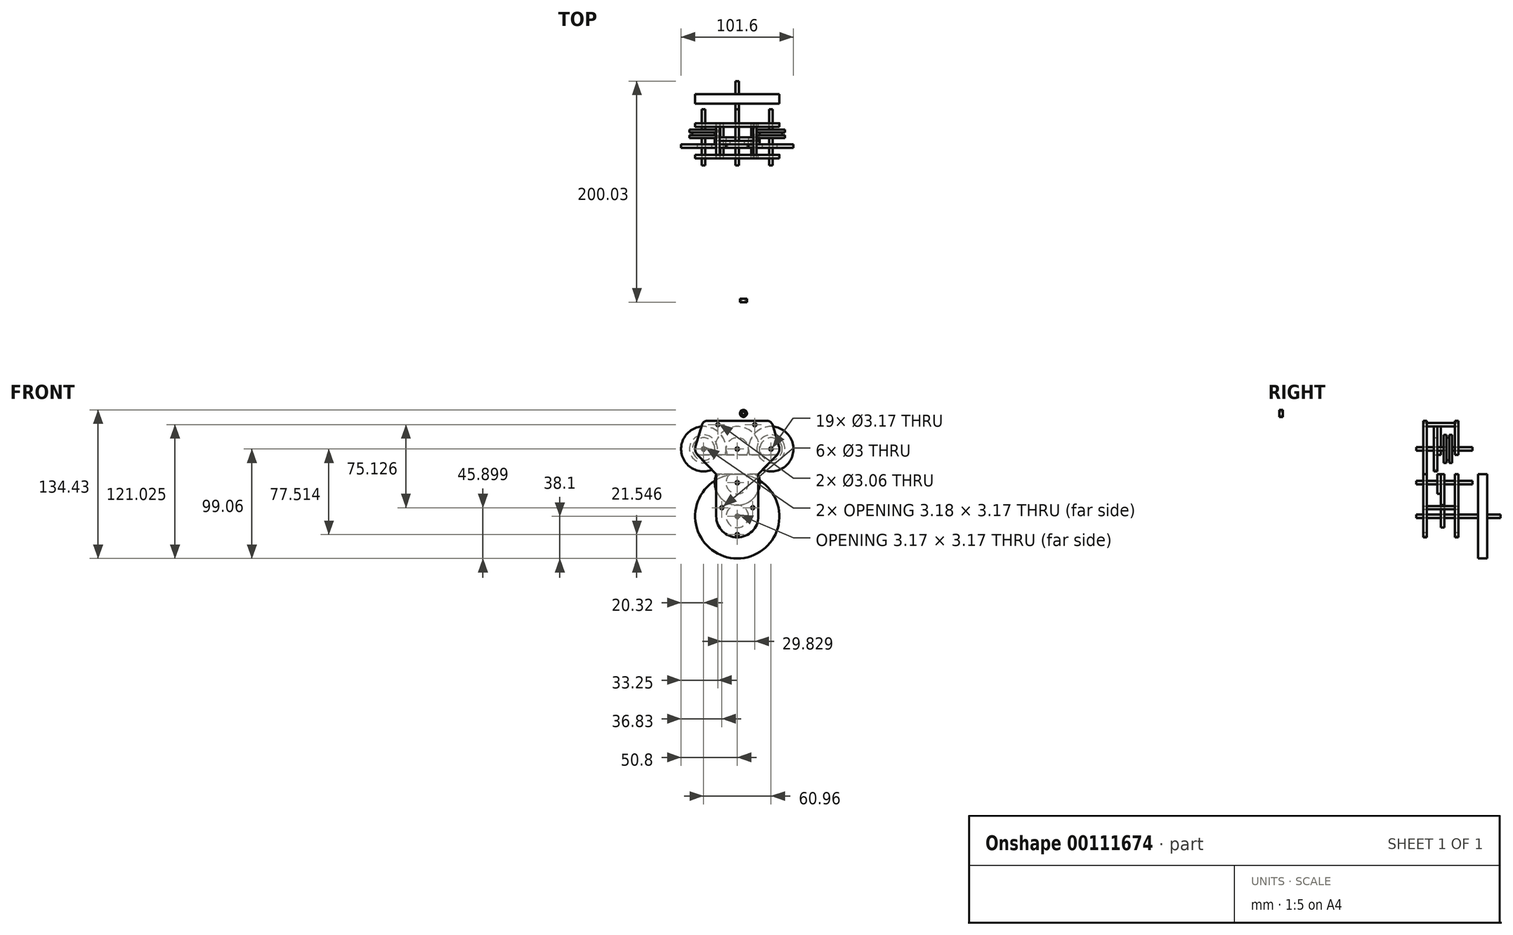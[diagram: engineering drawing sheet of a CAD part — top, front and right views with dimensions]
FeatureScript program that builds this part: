
annotation { "Feature Type Name" : "Feature", "Feature Type Description" : "" }
export const myFeature = defineFeature(function(context is Context, id is Id, definition is map)
    precondition{}
    {
        {
            var Q0;
            Q0=qCreatedBy(makeId("Front.planeOp"),FACE);
            var sketch = newSketch(context, id + "F0", { "sketchPlane" : qUnion([Q0])});
            skLineSegment(sketch, "E0", {"start": v(0, 0) * mm, "end": v(0, -60.96) * mm});
            skCircle(sketch, "E1", {"center": v(0, -60.96) * mm, "radius": 10.16 * mm});
            skCircle(sketch, "E2", {"center": v(0, -30.48) * mm, "radius": 20.32 * mm});
            skCircle(sketch, "E3", {"center": v(0, -30.48) * mm, "radius": 10.16 * mm});
            skCircle(sketch, "E4", {"center": v(0, 0) * mm, "radius": 20.32 * mm});
            skCircle(sketch, "E5", {"center": v(0, 0) * mm, "radius": 10.16 * mm});
            skLineSegment(sketch, "E6", {"start": v(0, 0) * mm, "end": v(30.48, 0) * mm});
            skLineSegment(sketch, "E7", {"start": v(30.48, 0) * mm, "end": v(-30.48, 0) * mm});
            skCircle(sketch, "E8", {"center": v(-30.48, 0) * mm, "radius": 20.32 * mm});
            skCircle(sketch, "E9", {"center": v(30.48, 0) * mm, "radius": 20.32 * mm});
            skCircle(sketch, "E10", {"center": v(-30.48, 0) * mm, "radius": 1.59 * mm});
            skCircle(sketch, "E11", {"center": v(0, 0) * mm, "radius": 1.59 * mm});
            skCircle(sketch, "E12", {"center": v(30.48, 0) * mm, "radius": 1.59 * mm});
            skCircle(sketch, "E13", {"center": v(0, -30.48) * mm, "radius": 1.59 * mm});
            skCircle(sketch, "E14", {"center": v(0, -60.96) * mm, "radius": 1.59 * mm});
            skSolve(sketch);
        }
        {
            var Q0;
            Q0=qCreatedBy(makeId("Front.planeOp"),FACE);
            cPlane(context, id + "F1", {"entities" : qUnion([Q0]), "cplaneType" : CPlaneType.OFFSET, "offset" : 3.17 * mm, "width" : 152.4 * mm, "height" : 152.4 * mm});
        }
        {
            var Q0;
            Q0=qCreatedBy(id+"F1.planeOp",FACE);
            var sketch = newSketch(context, id + "F2", { "sketchPlane" : qUnion([Q0])});
            skCircle(sketch, "E15.0", {"center": v(0, 0) * mm, "radius": 1.59 * mm});
            skCircle(sketch, "E16.0", {"center": v(30.48, 0) * mm, "radius": 1.59 * mm});
            skCircle(sketch, "E17.0", {"center": v(-30.48, 0) * mm, "radius": 1.59 * mm});
            skCircle(sketch, "E18.0", {"center": v(0, -30.48) * mm, "radius": 1.59 * mm});
            skCircle(sketch, "E19.0", {"center": v(0, -60.96) * mm, "radius": 1.59 * mm});
            skLineSegment(sketch, "E20", {"start": v(-30.9, 25.53) * mm, "end": v(30.73, 25.48) * mm});
            skCircle(sketch, "E21", {"center": v(0, -60.96) * mm, "radius": 19.05 * mm});
            skLineSegment(sketch, "E22", {"start": v(0, -60.96) * mm, "end": v(-19.05, -60.96) * mm});
            skLineSegment(sketch, "E23", {"start": v(0, -60.96) * mm, "end": v(19.05, -60.96) * mm});
            skLineSegment(sketch, "E24", {"start": v(19.05, -60.96) * mm, "end": v(19.05, -22.68) * mm});
            skLineSegment(sketch, "E25", {"start": v(-19.05, -60.96) * mm, "end": v(-19.05, -22.68) * mm});
            skCircle(sketch, "E26", {"center": v(30.48, 0) * mm, "radius": 7.62 * mm});
            skCircle(sketch, "E27", {"center": v(-30.48, 0) * mm, "radius": 7.62 * mm});
            skLineSegment(sketch, "E28", {"start": v(37.77, 2.2) * mm, "end": v(30.73, 25.48) * mm});
            skLineSegment(sketch, "E29", {"start": v(-30.9, 25.53) * mm, "end": v(-37.79, 2.15) * mm});
            skLineSegment(sketch, "E30", {"start": v(-35.94, -5.31) * mm, "end": v(-19.05, -22.68) * mm});
            skLineSegment(sketch, "E31", {"start": v(19.05, -22.68) * mm, "end": v(35.94, -5.31) * mm});
            skLineSegment(sketch, "E32", {"start": v(-0.09, 25.5) * mm, "end": v(0, 0) * mm});
            skCircle(sketch, "E33", {"center": v(15.86, 21.96) * mm, "radius": 1.5 * mm});
            skCircle(sketch, "E34", {"center": v(-17.55, 21.96) * mm, "radius": 1.5 * mm});
            skLineSegment(sketch, "E35", {"start": v(0, -53.16) * mm, "end": v(13.97, -53.16) * mm});
            skLineSegment(sketch, "E36", {"start": v(0, -53.16) * mm, "end": v(-13.97, -53.16) * mm});
            skCircle(sketch, "E37", {"center": v(13.97, -53.16) * mm, "radius": 1.5 * mm});
            skCircle(sketch, "E38", {"center": v(-13.97, -53.16) * mm, "radius": 1.5 * mm});
            skSolve(sketch);
        }
        {
            var Q0;
            Q0 = qSketchRegion(id + "F2", true);
            extrude(context, id + "F3", {"entities" : qUnion([Q0]), "depth" : 3.17 * mm});
        }
        {
            var Q0;
            Q0=makeQuery(id+"F3.opExtrude","CAP_FACE",FACE,{"disambiguationData":[OSD([sQuery(id+"F2.wireOp",EDGE,"E15.0"),sQuery(id+"F2.wireOp",EDGE,"E16.0"),sQuery(id+"F2.wireOp",EDGE,"E17.0"),sQuery(id+"F2.wireOp",EDGE,"E18.0"),sQuery(id+"F2.wireOp",EDGE,"E19.0"),sQuery(id+"F2.wireOp",EDGE,"DBtKeoEe-sxFA-O8Cd-5S0k-6v0tE5dEFOVB"),sQuery(id+"F2.wireOp",EDGE,"FIhjvamt-jRJC-0Qks-E5rB-tkHqEzlwZ8Zz"),sQuery(id+"F2.wireOp",EDGE,"KFKZsqRK-ZnOK-MkHf-qwN2-OSyO8BWJYoXi"),sQuery(id+"F2.wireOp",EDGE,"E20"),sQuery(id+"F2.wireOp",EDGE,"WcMJ8zR9-ZSbF-q2kM-oJpC-Lqe6jbKvmUBf"),sQuery(id+"F2.wireOp",EDGE,"RShMeTTQ-3lLB-r0UE-RSKj-mqnAByZPcrAj")])],"isStart":false});
            cPlane(context, id + "F4", {"entities" : qUnion([Q0]), "cplaneType" : CPlaneType.OFFSET, "offset" : 25.4 * mm, "width" : 152.4 * mm, "height" : 152.4 * mm});
        }
        {
            var Q0;
            Q0=qCreatedBy(id+"F4.planeOp",FACE);
            var sketch = newSketch(context, id + "F5", { "sketchPlane" : qUnion([Q0])});
            skCircle(sketch, "E39.0", {"center": v(-30.48, 0) * mm, "radius": 1.59 * mm});
            skCircle(sketch, "E40.0", {"center": v(0, 0) * mm, "radius": 1.59 * mm});
            skCircle(sketch, "E41.0", {"center": v(30.48, 0) * mm, "radius": 1.59 * mm});
            skCircle(sketch, "E42.0", {"center": v(0, -30.48) * mm, "radius": 1.59 * mm});
            skCircle(sketch, "E43.0", {"center": v(0, -60.96) * mm, "radius": 1.59 * mm});
            skLineSegment(sketch, "E44.0", {"start": v(19.05, -60.96) * mm, "end": v(19.05, -22.68) * mm});
            skArc(sketch, "E45.0", {"start": v(-19.05, -60.96) * mm, "mid": v(0, -80) * mm, "end": v(19.05, -60.96) * mm});
            skLineSegment(sketch, "E46.0", {"start": v(-19.05, -60.96) * mm, "end": v(-19.05, -22.68) * mm});
            skLineSegment(sketch, "E47.0", {"start": v(-35.94, -5.31) * mm, "end": v(-19.05, -22.68) * mm});
            skArc(sketch, "E48.0", {"start": v(-37.79, 2.15) * mm, "mid": v(-37.88, -1.83) * mm, "end": v(-35.94, -5.31) * mm});
            skLineSegment(sketch, "E49.0", {"start": v(-30.9, 25.53) * mm, "end": v(-37.79, 2.15) * mm});
            skLineSegment(sketch, "E50.0", {"start": v(-30.9, 25.53) * mm, "end": v(30.73, 25.48) * mm});
            skLineSegment(sketch, "E51.0", {"start": v(37.77, 2.2) * mm, "end": v(30.73, 25.48) * mm});
            skLineSegment(sketch, "E52.0", {"start": v(19.05, -22.68) * mm, "end": v(35.94, -5.31) * mm});
            skArc(sketch, "E53.0", {"start": v(35.94, -5.31) * mm, "mid": v(37.88, -1.8) * mm, "end": v(37.77, 2.2) * mm});
            skCircle(sketch, "E54.0", {"center": v(-17.55, 21.96) * mm, "radius": 1.5 * mm});
            skCircle(sketch, "E55.0", {"center": v(15.86, 21.96) * mm, "radius": 1.5 * mm});
            skCircle(sketch, "E56.0", {"center": v(-13.97, -53.16) * mm, "radius": 1.5 * mm});
            skCircle(sketch, "E57.0", {"center": v(13.97, -53.16) * mm, "radius": 1.5 * mm});
            skSolve(sketch);
        }
        {
            var Q0;
            Q0 = qSketchRegion(id + "F5", true);
            extrude(context, id + "F6", {"entities" : qUnion([Q0]), "depth" : 3.17 * mm});
        }
        {
            var Q0;
            Q0=makeQuery(id+"F2.imprint","IMPRINT",FACE,{"disambiguationData":[TD([[makeQuery(id+"F2.imprint","IMPRINT",EDGE,{"derivedFrom":sQuery(id+"F2.wireOp",EDGE,"E33")}),1.0]])]});
            extrude(context, id + "F7", {"entities" : qUnion([Q0]), "depth" : 0.25 * mm});
        }
        {
            var Q0;
            Q0=makeQuery(id+"F7.opExtrude","CAP_FACE",FACE,{"disambiguationData":[OSD([sQuery(id+"F2.wireOp",EDGE,"E33")])],"isStart":true});
            extrude(context, id + "F8", {"entities" : qUnion([Q0]), "operationType" : NewBodyOperationType.REMOVE, "oppositeDirection" : true, "depth" : 25.4 * mm});
        }
        {
            var Q0;
            Q0=makeQuery(id+"F3.opExtrude","CAP_FACE",FACE,{"disambiguationData":[OSD([sQuery(id+"F2.wireOp",EDGE,"E15.0"),sQuery(id+"F2.wireOp",EDGE,"E16.0"),sQuery(id+"F2.wireOp",EDGE,"E17.0"),sQuery(id+"F2.wireOp",EDGE,"E18.0"),sQuery(id+"F2.wireOp",EDGE,"E19.0"),sQuery(id+"F2.wireOp",EDGE,"E20"),sQuery(id+"F2.wireOp",EDGE,"E21"),sQuery(id+"F2.wireOp",EDGE,"E24"),sQuery(id+"F2.wireOp",EDGE,"E25"),sQuery(id+"F2.wireOp",EDGE,"E26"),sQuery(id+"F2.wireOp",EDGE,"E27"),sQuery(id+"F2.wireOp",EDGE,"E28"),sQuery(id+"F2.wireOp",EDGE,"E29"),sQuery(id+"F2.wireOp",EDGE,"E30"),sQuery(id+"F2.wireOp",EDGE,"E31"),sQuery(id+"F2.wireOp",EDGE,"E33"),sQuery(id+"F2.wireOp",EDGE,"E34"),sQuery(id+"F2.wireOp",EDGE,"E37"),sQuery(id+"F2.wireOp",EDGE,"E38")])],"isStart":true});
            cPlane(context, id + "F9", {"entities" : qUnion([Q0]), "cplaneType" : CPlaneType.OFFSET, "offset" : 7.62 * mm, "width" : 152.4 * mm, "height" : 152.4 * mm});
        }
        {
            var Q0;
            Q0=makeQuery(id+"F6.opExtrude","CAP_FACE",FACE,{"disambiguationData":[OSD([sQuery(id+"F5.wireOp",EDGE,"E39.0"),sQuery(id+"F5.wireOp",EDGE,"E40.0"),sQuery(id+"F5.wireOp",EDGE,"E41.0"),sQuery(id+"F5.wireOp",EDGE,"E42.0"),sQuery(id+"F5.wireOp",EDGE,"E43.0"),sQuery(id+"F5.wireOp",EDGE,"E44.0"),sQuery(id+"F5.wireOp",EDGE,"E45.0"),sQuery(id+"F5.wireOp",EDGE,"E46.0"),sQuery(id+"F5.wireOp",EDGE,"E47.0"),sQuery(id+"F5.wireOp",EDGE,"E48.0"),sQuery(id+"F5.wireOp",EDGE,"E49.0"),sQuery(id+"F5.wireOp",EDGE,"E50.0"),sQuery(id+"F5.wireOp",EDGE,"E51.0"),sQuery(id+"F5.wireOp",EDGE,"E52.0"),sQuery(id+"F5.wireOp",EDGE,"E53.0"),sQuery(id+"F5.wireOp",EDGE,"E54.0"),sQuery(id+"F5.wireOp",EDGE,"E55.0"),sQuery(id+"F5.wireOp",EDGE,"E56.0"),sQuery(id+"F5.wireOp",EDGE,"E57.0")])],"isStart":true});
            cPlane(context, id + "F10", {"entities" : qUnion([Q0]), "cplaneType" : CPlaneType.OFFSET, "offset" : 12.7 * mm, "width" : 152.4 * mm, "height" : 152.4 * mm});
        }
        {
            var Q0;
            Q0=qCreatedBy(id+"F10.planeOp",FACE);
            var sketch = newSketch(context, id + "F11", { "sketchPlane" : qUnion([Q0])});
            skCircle(sketch, "E58.0", {"center": v(0, -30.48) * mm, "radius": 1.59 * mm});
            skCircle(sketch, "E59.0", {"center": v(0, -60.96) * mm, "radius": 1.59 * mm});
            skCircle(sketch, "E60.0", {"center": v(0, -60.96) * mm, "radius": 10.16 * mm});
            skCircle(sketch, "E61.0", {"center": v(0, -30.48) * mm, "radius": 20.32 * mm});
            skSolve(sketch);
        }
        {
            var Q0;
            Q0 = qSketchRegion(id + "F11", true);
            extrude(context, id + "F12", {"entities" : qUnion([Q0]), "depth" : 3.17 * mm});
        }
        {
            var Q0;
            Q0=makeQuery(id+"F12.opExtrude","CAP_FACE",FACE,{"disambiguationData":[OSD([sQuery(id+"F11.wireOp",EDGE,"E58.0"),sQuery(id+"F11.wireOp",EDGE,"E61.0")])],"isStart":true});
            var sketch = newSketch(context, id + "F13", { "sketchPlane" : qUnion([Q0])});
            skCircle(sketch, "E62.0", {"center": v(0, -30.48) * mm, "radius": 10.16 * mm});
            skCircle(sketch, "E63.0", {"center": v(0, -30.48) * mm, "radius": 1.59 * mm});
            skCircle(sketch, "E64.0", {"center": v(0, 0) * mm, "radius": 1.59 * mm});
            skCircle(sketch, "E65.0", {"center": v(0, 0) * mm, "radius": 20.32 * mm});
            skSolve(sketch);
        }
        {
            var Q0;
            Q0 = qSketchRegion(id + "F13", true);
            extrude(context, id + "F14", {"entities" : qUnion([Q0]), "depth" : 3.17 * mm});
        }
        {
            var Q0;
            Q0=makeQuery(id+"F14.opExtrude","CAP_FACE",FACE,{"disambiguationData":[OSD([sQuery(id+"F13.wireOp",EDGE,"E64.0"),sQuery(id+"F13.wireOp",EDGE,"E65.0")])],"isStart":false});
            var sketch = newSketch(context, id + "F15", { "sketchPlane" : qUnion([Q0])});
            skCircle(sketch, "E66.0", {"center": v(30.48, 0) * mm, "radius": 20.32 * mm});
            skCircle(sketch, "E67.0", {"center": v(0, 0) * mm, "radius": 10.16 * mm});
            skCircle(sketch, "E68.0", {"center": v(-30.48, 0) * mm, "radius": 20.32 * mm});
            skCircle(sketch, "E69.0", {"center": v(0, 0) * mm, "radius": 1.59 * mm});
            skCircle(sketch, "E70.0", {"center": v(30.48, 0) * mm, "radius": 1.59 * mm});
            skCircle(sketch, "E71.0", {"center": v(-30.48, 0) * mm, "radius": 1.59 * mm});
            skSolve(sketch);
        }
        {
            var Q0;
            Q0 = qSketchRegion(id + "F15", true);
            extrude(context, id + "F16", {"entities" : qUnion([Q0]), "depth" : 3.17 * mm});
        }
        {
            var Q0;
            Q0=makeQuery(id+"F3.opExtrude","CAP_FACE",FACE,{"disambiguationData":[OSD([sQuery(id+"F2.wireOp",EDGE,"E15.0"),sQuery(id+"F2.wireOp",EDGE,"E16.0"),sQuery(id+"F2.wireOp",EDGE,"E17.0"),sQuery(id+"F2.wireOp",EDGE,"E18.0"),sQuery(id+"F2.wireOp",EDGE,"E19.0"),sQuery(id+"F2.wireOp",EDGE,"E20"),sQuery(id+"F2.wireOp",EDGE,"E21"),sQuery(id+"F2.wireOp",EDGE,"E24"),sQuery(id+"F2.wireOp",EDGE,"E25"),sQuery(id+"F2.wireOp",EDGE,"E26"),sQuery(id+"F2.wireOp",EDGE,"E27"),sQuery(id+"F2.wireOp",EDGE,"E28"),sQuery(id+"F2.wireOp",EDGE,"E29"),sQuery(id+"F2.wireOp",EDGE,"E30"),sQuery(id+"F2.wireOp",EDGE,"E31"),sQuery(id+"F2.wireOp",EDGE,"E33"),sQuery(id+"F2.wireOp",EDGE,"E34"),sQuery(id+"F2.wireOp",EDGE,"E37"),sQuery(id+"F2.wireOp",EDGE,"E38")])],"isStart":true});
            var sketch = newSketch(context, id + "F17", { "sketchPlane" : qUnion([Q0])});
            skLineSegment(sketch, "E72.0", {"start": v(-19.05, -22.68) * mm, "end": v(-35.94, -5.31) * mm});
            skLineSegment(sketch, "E73.0", {"start": v(35.94, -5.31) * mm, "end": v(19.05, -22.68) * mm});
            skLineSegment(sketch, "E74", {"start": v(35.94, -5.31) * mm, "end": v(-35.94, -5.31) * mm});
            skLineSegment(sketch, "E75", {"start": v(-19.05, -22.68) * mm, "end": v(19.05, -22.68) * mm});
            skSolve(sketch);
        }
        {
            var Q0;
            Q0 = qSketchRegion(id + "F17", true);
            extrude(context, id + "F18", {"entities" : qUnion([Q0]), "operationType" : NewBodyOperationType.REMOVE, "oppositeDirection" : true, "depth" : 25.4 * mm});
        }
        {
            var Q0;
            {var subQ0=sQuery(id+"F2.wireOp",EDGE,"E24");Q0=makeQuery(id+"F18.boolean.opBoolean","MERGE",EDGE,{"derivedFrom":[makeQuery(id+"F3.opExtrude","SWEPT_EDGE",EDGE,{"disambiguationData":[OSD([subQ0,sQuery(id+"F2.wireOp",EDGE,"E31")])]}),makeQuery(id+"F18.opExtrude","SWEPT_EDGE",EDGE,{"disambiguationData":[OSD([subQ0,sQuery(id+"F17.wireOp",EDGE,"E72.0"),sQuery(id+"F17.wireOp",EDGE,"E75")])]})]});}
            var Q1;
            {var subQ0=sQuery(id+"F2.wireOp",EDGE,"E25");Q1=makeQuery(id+"F18.boolean.opBoolean","MERGE",EDGE,{"derivedFrom":[makeQuery(id+"F3.opExtrude","SWEPT_EDGE",EDGE,{"disambiguationData":[OSD([subQ0,sQuery(id+"F2.wireOp",EDGE,"E30")])]}),makeQuery(id+"F18.opExtrude","SWEPT_EDGE",EDGE,{"disambiguationData":[OSD([subQ0,sQuery(id+"F17.wireOp",EDGE,"E73.0"),sQuery(id+"F17.wireOp",EDGE,"E75")])]})]});}
            var Q2;
            {var subQ0=sQuery(id+"F2.wireOp",EDGE,"E27");Q2=makeQuery(id+"F18.boolean.opBoolean","MERGE",EDGE,{"derivedFrom":[makeQuery(id+"F3.opExtrude","SWEPT_EDGE",EDGE,{"disambiguationData":[OSD([subQ0,sQuery(id+"F2.wireOp",EDGE,"E30")])]}),makeQuery(id+"F18.opExtrude","SWEPT_EDGE",EDGE,{"disambiguationData":[OSD([subQ0,sQuery(id+"F17.wireOp",EDGE,"E73.0"),sQuery(id+"F17.wireOp",EDGE,"E74")])]})]});}
            var Q3;
            {var subQ0=sQuery(id+"F2.wireOp",EDGE,"E26");Q3=makeQuery(id+"F18.boolean.opBoolean","MERGE",EDGE,{"derivedFrom":[makeQuery(id+"F3.opExtrude","SWEPT_EDGE",EDGE,{"disambiguationData":[OSD([subQ0,sQuery(id+"F2.wireOp",EDGE,"E31")])]}),makeQuery(id+"F18.opExtrude","SWEPT_EDGE",EDGE,{"disambiguationData":[OSD([subQ0,sQuery(id+"F17.wireOp",EDGE,"E72.0"),sQuery(id+"F17.wireOp",EDGE,"E74")])]})]});}
            fillet(context, id + "F19", {"entities" : qUnion([Q0, Q1, Q2, Q3]), "radius" : 5.08 * mm, "tangentPropagation" : true, "allowEdgeOverflow" : false});
        }
        {
            var Q0;
            Q0=makeQuery(id+"F3.opExtrude","SWEPT_EDGE",EDGE,{"disambiguationData":[OSD([sQuery(id+"F2.wireOp",EDGE,"E20"),sQuery(id+"F2.wireOp",EDGE,"E28")])]});
            var Q1;
            Q1=makeQuery(id+"F3.opExtrude","SWEPT_EDGE",EDGE,{"disambiguationData":[OSD([sQuery(id+"F2.wireOp",EDGE,"E20"),sQuery(id+"F2.wireOp",EDGE,"E29")])]});
            var Q2;
            Q2=makeQuery(id+"F6.opExtrude","SWEPT_EDGE",EDGE,{"disambiguationData":[OSD([sQuery(id+"F5.wireOp",EDGE,"E50.0"),sQuery(id+"F5.wireOp",EDGE,"E51.0")])]});
            var Q3;
            Q3=makeQuery(id+"F6.opExtrude","SWEPT_EDGE",EDGE,{"disambiguationData":[OSD([sQuery(id+"F5.wireOp",EDGE,"E49.0"),sQuery(id+"F5.wireOp",EDGE,"E50.0")])]});
            fillet(context, id + "F20", {"entities" : qUnion([Q0, Q1, Q2, Q3]), "radius" : 5.08 * mm, "tangentPropagation" : true, "allowEdgeOverflow" : false});
        }
        {
            var Q0;
            Q0=makeQuery(id+"F6.opExtrude","CAP_FACE",FACE,{"disambiguationData":[OSD([sQuery(id+"F5.wireOp",EDGE,"E39.0"),sQuery(id+"F5.wireOp",EDGE,"E40.0"),sQuery(id+"F5.wireOp",EDGE,"E41.0"),sQuery(id+"F5.wireOp",EDGE,"E42.0"),sQuery(id+"F5.wireOp",EDGE,"E43.0"),sQuery(id+"F5.wireOp",EDGE,"E44.0"),sQuery(id+"F5.wireOp",EDGE,"E45.0"),sQuery(id+"F5.wireOp",EDGE,"E46.0"),sQuery(id+"F5.wireOp",EDGE,"E47.0"),sQuery(id+"F5.wireOp",EDGE,"E48.0"),sQuery(id+"F5.wireOp",EDGE,"E49.0"),sQuery(id+"F5.wireOp",EDGE,"E50.0"),sQuery(id+"F5.wireOp",EDGE,"E51.0"),sQuery(id+"F5.wireOp",EDGE,"E52.0"),sQuery(id+"F5.wireOp",EDGE,"E53.0"),sQuery(id+"F5.wireOp",EDGE,"E54.0"),sQuery(id+"F5.wireOp",EDGE,"E55.0"),sQuery(id+"F5.wireOp",EDGE,"E56.0"),sQuery(id+"F5.wireOp",EDGE,"E57.0")])],"isStart":false});
            cPlane(context, id + "F21", {"entities" : qUnion([Q0]), "cplaneType" : CPlaneType.OFFSET, "offset" : 6.35 * mm, "width" : 152.4 * mm, "height" : 152.4 * mm});
        }
        {
            var Q0;
            Q0=qCreatedBy(id+"F21.planeOp",FACE);
            var sketch = newSketch(context, id + "F22", { "sketchPlane" : qUnion([Q0])});
            skCircle(sketch, "E76.0", {"center": v(-30.48, 0) * mm, "radius": 1.59 * mm});
            skCircle(sketch, "E77.0", {"center": v(0, 0) * mm, "radius": 1.59 * mm});
            skCircle(sketch, "E78.0", {"center": v(30.48, 0) * mm, "radius": 1.59 * mm});
            skCircle(sketch, "E79.0", {"center": v(0, -30.48) * mm, "radius": 1.59 * mm});
            skCircle(sketch, "E80.0", {"center": v(0, -60.96) * mm, "radius": 1.59 * mm});
            skSolve(sketch);
        }
        {
            var Q0;
            Q0 = qSketchRegion(id + "F22", true);
            extrude(context, id + "F23", {"entities" : qUnion([Q0]), "oppositeDirection" : true, "depth" : 50.8 * mm});
        }
        {
            var Q0;
            Q0=makeQuery(id+"F6.opExtrude","CAP_FACE",FACE,{"disambiguationData":[OSD([sQuery(id+"F5.wireOp",EDGE,"E39.0"),sQuery(id+"F5.wireOp",EDGE,"E40.0"),sQuery(id+"F5.wireOp",EDGE,"E41.0"),sQuery(id+"F5.wireOp",EDGE,"E42.0"),sQuery(id+"F5.wireOp",EDGE,"E43.0"),sQuery(id+"F5.wireOp",EDGE,"E44.0"),sQuery(id+"F5.wireOp",EDGE,"E45.0"),sQuery(id+"F5.wireOp",EDGE,"E46.0"),sQuery(id+"F5.wireOp",EDGE,"E47.0"),sQuery(id+"F5.wireOp",EDGE,"E48.0"),sQuery(id+"F5.wireOp",EDGE,"E49.0"),sQuery(id+"F5.wireOp",EDGE,"E50.0"),sQuery(id+"F5.wireOp",EDGE,"E51.0"),sQuery(id+"F5.wireOp",EDGE,"E52.0"),sQuery(id+"F5.wireOp",EDGE,"E53.0"),sQuery(id+"F5.wireOp",EDGE,"E54.0"),sQuery(id+"F5.wireOp",EDGE,"E55.0"),sQuery(id+"F5.wireOp",EDGE,"E56.0"),sQuery(id+"F5.wireOp",EDGE,"E57.0")])],"isStart":false});
            var sketch = newSketch(context, id + "F24", { "sketchPlane" : qUnion([Q0])});
            skCircle(sketch, "E81.0", {"center": v(-17.55, 21.96) * mm, "radius": 1.5 * mm});
            skCircle(sketch, "E82.0", {"center": v(15.86, 21.96) * mm, "radius": 1.5 * mm});
            skCircle(sketch, "E83.0", {"center": v(-13.97, -53.16) * mm, "radius": 1.5 * mm});
            skCircle(sketch, "E84.0", {"center": v(13.97, -53.16) * mm, "radius": 1.5 * mm});
            skLineSegment(sketch, "E85", {"start": v(0, -80) * mm, "end": v(0, -62.55) * mm});
            skLineSegment(sketch, "E86", {"start": v(0, -77.51) * mm, "end": v(-9.43, -77.51) * mm});
            skLineSegment(sketch, "E87", {"start": v(-9.43, -77.51) * mm, "end": v(9.43, -77.51) * mm});
            skCircle(sketch, "E88", {"center": v(0, -77.51) * mm, "radius": 1.59 * mm});
            skCircle(sketch, "E89", {"center": v(-17.55, 21.96) * mm, "radius": 1.53 * mm});
            skSolve(sketch);
        }
        {
            var Q0;
            Q0 = qSketchRegion(id + "F24", true);
            extrude(context, id + "F25", {"entities" : qUnion([Q0]), "operationType" : NewBodyOperationType.REMOVE, "endBound" : BoundingType.THROUGH_ALL, "oppositeDirection" : true, "depth" : 38.1 * mm});
        }
        {
            var Q0;
            Q0=makeQuery(id+"F23.opExtrude","CAP_FACE",FACE,{"disambiguationData":[OSD([sQuery(id+"F22.wireOp",EDGE,"E80.0")])],"isStart":false});
            extrude(context, id + "F26", {"entities" : qUnion([Q0]), "operationType" : NewBodyOperationType.ADD, "depth" : 25.4 * mm});
        }
        {
            var Q0;
            {var subQ0=sQuery(id+"F2.wireOp",EDGE,"E24");var subQ1=sQuery(id+"F2.wireOp",EDGE,"E21");var subQ2=sQuery(id+"F2.wireOp",EDGE,"E19.0");var subQ3=sQuery(id+"F2.wireOp",EDGE,"E18.0");var subQ4=sQuery(id+"F2.wireOp",EDGE,"E25");var subQ5=sQuery(id+"F2.wireOp",EDGE,"E37");var subQ6=sQuery(id+"F2.wireOp",EDGE,"E38");Q0=makeQuery(id+"F18.boolean.opBoolean","SPLIT",FACE,{"disambiguationData":[TD([makeQuery(id+"F3.opExtrude","SWEPT_FACE",FACE,{"disambiguationData":[OSD([subQ3])]})])],"derivedFrom":makeQuery(id+"F3.opExtrude","CAP_FACE",FACE,{"disambiguationData":[OSD([sQuery(id+"F2.wireOp",EDGE,"E15.0"),sQuery(id+"F2.wireOp",EDGE,"E16.0"),sQuery(id+"F2.wireOp",EDGE,"E17.0"),subQ3,subQ2,sQuery(id+"F2.wireOp",EDGE,"E20"),subQ1,subQ0,subQ4,sQuery(id+"F2.wireOp",EDGE,"E26"),sQuery(id+"F2.wireOp",EDGE,"E27"),sQuery(id+"F2.wireOp",EDGE,"E28"),sQuery(id+"F2.wireOp",EDGE,"E29"),sQuery(id+"F2.wireOp",EDGE,"E30"),sQuery(id+"F2.wireOp",EDGE,"E31"),sQuery(id+"F2.wireOp",EDGE,"E33"),sQuery(id+"F2.wireOp",EDGE,"E34"),subQ5,subQ6])],"isStart":true})});}
            cPlane(context, id + "F27", {"entities" : qUnion([Q0]), "cplaneType" : CPlaneType.OFFSET, "offset" : 17.78 * mm, "width" : 152.4 * mm, "height" : 152.4 * mm});
        }
        {
            var Q0;
            Q0=qCreatedBy(id+"F27.planeOp",FACE);
            var sketch = newSketch(context, id + "F28", { "sketchPlane" : qUnion([Q0])});
            skCircle(sketch, "E90.0", {"center": v(0, -60.96) * mm, "radius": 1.59 * mm});
            skCircle(sketch, "E91", {"center": v(0, -60.96) * mm, "radius": 38.1 * mm});
            skLineSegment(sketch, "E92", {"start": v(0, -60.96) * mm, "end": v(-38.1, -60.96) * mm});
            skSolve(sketch);
        }
        {
            var Q0;
            Q0=makeQuery(id+"F28.imprint","IMPRINT",FACE,{"disambiguationData":[TD([[makeQuery(id+"F28.imprint","IMPRINT",EDGE,{"derivedFrom":sQuery(id+"F28.wireOp",EDGE,"E90.0")}),-1.0]])]});
            extrude(context, id + "F29", {"entities" : qUnion([Q0]), "operationType" : NewBodyOperationType.ADD, "depth" : 8.47 * mm});
        }
        {
            var Q0;
            Q0=makeQuery(id+"F14.opExtrude","CAP_FACE",FACE,{"disambiguationData":[OSD([sQuery(id+"F13.wireOp",EDGE,"E64.0"),sQuery(id+"F13.wireOp",EDGE,"E65.0")])],"isStart":true});
            cPlane(context, id + "F30", {"entities" : qUnion([Q0]), "cplaneType" : CPlaneType.OFFSET, "offset" : 2.54 * mm, "width" : 152.4 * mm, "height" : 152.4 * mm});
        }
        {
            var Q0;
            Q0=qCreatedBy(id+"F30.planeOp",FACE);
            var sketch = newSketch(context, id + "F31", { "sketchPlane" : qUnion([Q0])});
            skCircle(sketch, "E93.0", {"center": v(-30.48, 0) * mm, "radius": 1.59 * mm});
            skCircle(sketch, "E94.0", {"center": v(30.48, 0) * mm, "radius": 1.59 * mm});
            skCircle(sketch, "E95", {"center": v(-30.48, 0) * mm, "radius": 12.7 * mm});
            skCircle(sketch, "E96", {"center": v(30.48, 0) * mm, "radius": 12.7 * mm});
            skSolve(sketch);
        }
        {
            var Q0;
            Q0 = qSketchRegion(id + "F31", true);
            extrude(context, id + "F32", {"entities" : qUnion([Q0]), "depth" : 2.54 * mm});
        }
        {
            var Q0;
            Q0=makeQuery(id+"F32.opExtrude","CAP_FACE",FACE,{"disambiguationData":[OSD([sQuery(id+"F31.wireOp",EDGE,"E93.0"),sQuery(id+"F31.wireOp",EDGE,"E95")])],"isStart":false});
            var sketch = newSketch(context, id + "F33", { "sketchPlane" : qUnion([Q0])});
            skCircle(sketch, "E97.0", {"center": v(-30.48, 0) * mm, "radius": 1.59 * mm});
            skCircle(sketch, "E98.0", {"center": v(30.48, 0) * mm, "radius": 1.59 * mm});
            skCircle(sketch, "E99", {"center": v(30.48, 0) * mm, "radius": 10.16 * mm});
            skCircle(sketch, "E100", {"center": v(-30.48, 0) * mm, "radius": 10.16 * mm});
            skSolve(sketch);
        }
        {
            var Q0;
            Q0 = qSketchRegion(id + "F33", true);
            extrude(context, id + "F34", {"entities" : qUnion([Q0]), "operationType" : NewBodyOperationType.ADD, "depth" : 2.54 * mm});
        }
        {
            var Q0;
            Q0=makeQuery(id+"F34.opExtrude","CAP_FACE",FACE,{"disambiguationData":[OSD([sQuery(id+"F33.wireOp",EDGE,"E97.0"),sQuery(id+"F33.wireOp",EDGE,"E100")])],"isStart":false});
            var sketch = newSketch(context, id + "F35", { "sketchPlane" : qUnion([Q0])});
            skCircle(sketch, "E101.0", {"center": v(-30.48, 0) * mm, "radius": 1.59 * mm});
            skCircle(sketch, "E102.0", {"center": v(30.48, 0) * mm, "radius": 1.59 * mm});
            skCircle(sketch, "E103", {"center": v(-30.48, 0) * mm, "radius": 12.7 * mm});
            skCircle(sketch, "E104", {"center": v(30.48, 0) * mm, "radius": 12.7 * mm});
            skSolve(sketch);
        }
        {
            var Q0;
            Q0 = qSketchRegion(id + "F35", true);
            extrude(context, id + "F36", {"entities" : qUnion([Q0]), "operationType" : NewBodyOperationType.ADD, "depth" : 2.54 * mm});
        }
        {
            var Q0;
            Q0=makeQuery(id+"F6.opExtrude","CAP_FACE",FACE,{"disambiguationData":[OSD([sQuery(id+"F5.wireOp",EDGE,"E39.0"),sQuery(id+"F5.wireOp",EDGE,"E40.0"),sQuery(id+"F5.wireOp",EDGE,"E41.0"),sQuery(id+"F5.wireOp",EDGE,"E42.0"),sQuery(id+"F5.wireOp",EDGE,"E43.0"),sQuery(id+"F5.wireOp",EDGE,"E44.0"),sQuery(id+"F5.wireOp",EDGE,"E45.0"),sQuery(id+"F5.wireOp",EDGE,"E46.0"),sQuery(id+"F5.wireOp",EDGE,"E47.0"),sQuery(id+"F5.wireOp",EDGE,"E48.0"),sQuery(id+"F5.wireOp",EDGE,"E49.0"),sQuery(id+"F5.wireOp",EDGE,"E50.0"),sQuery(id+"F5.wireOp",EDGE,"E51.0"),sQuery(id+"F5.wireOp",EDGE,"E52.0"),sQuery(id+"F5.wireOp",EDGE,"E53.0"),sQuery(id+"F5.wireOp",EDGE,"E54.0"),sQuery(id+"F5.wireOp",EDGE,"E55.0"),sQuery(id+"F5.wireOp",EDGE,"E56.0"),sQuery(id+"F5.wireOp",EDGE,"E57.0")])],"isStart":true});
            cPlane(context, id + "F37", {"entities" : qUnion([Q0]), "cplaneType" : CPlaneType.OFFSET, "offset" : 25.4 * mm, "width" : 152.4 * mm, "height" : 152.4 * mm});
        }
        {
            var Q0;
            Q0=qCreatedBy(id+"F37.planeOp",FACE);
            var sketch = newSketch(context, id + "F38", { "sketchPlane" : qUnion([Q0])});
            skCircle(sketch, "E105.0", {"center": v(-15.86, 21.96) * mm, "radius": 1.5 * mm});
            skCircle(sketch, "E106.0", {"center": v(17.55, 21.96) * mm, "radius": 1.5 * mm});
            skCircle(sketch, "E107.0", {"center": v(13.97, -53.16) * mm, "radius": 1.5 * mm});
            skCircle(sketch, "E108.0", {"center": v(-13.97, -53.16) * mm, "radius": 1.5 * mm});
            skSolve(sketch);
        }
        {
            var Q0;
            Q0 = qSketchRegion(id + "F38", true);
            extrude(context, id + "F39", {"entities" : qUnion([Q0]), "oppositeDirection" : true, "depth" : 25.4 * mm});
        }
        {
            var Q0;
            Q0=makeQuery(id+"F28.imprint","IMPRINT",FACE,{"disambiguationData":[TD([[makeQuery(id+"F28.imprint","IMPRINT",EDGE,{"derivedFrom":sQuery(id+"F28.wireOp",EDGE,"E90.0")}),-1.0]])]});
            extrude(context, id + "F40", {"entities" : qUnion([Q0]), "operationType" : NewBodyOperationType.ADD, "depth" : 3.17 * mm});
        }
        {
            var Q0;
            Q0=makeQuery(id+"F28.imprint","IMPRINT",FACE,{"disambiguationData":[TD([[makeQuery(id+"F28.imprint","IMPRINT",EDGE,{"derivedFrom":sQuery(id+"F28.wireOp",EDGE,"E90.0")}),-1.0]])]});
            extrude(context, id + "F41", {"entities" : qUnion([Q0]), "operationType" : NewBodyOperationType.ADD, "depth" : 3.17 * mm});
        }
        {
            var Q0;
            Q0=makeQuery(id+"F6.opExtrude","CAP_FACE",FACE,{"disambiguationData":[OSD([sQuery(id+"F5.wireOp",EDGE,"E39.0"),sQuery(id+"F5.wireOp",EDGE,"E40.0"),sQuery(id+"F5.wireOp",EDGE,"E41.0"),sQuery(id+"F5.wireOp",EDGE,"E42.0"),sQuery(id+"F5.wireOp",EDGE,"E43.0"),sQuery(id+"F5.wireOp",EDGE,"E44.0"),sQuery(id+"F5.wireOp",EDGE,"E45.0"),sQuery(id+"F5.wireOp",EDGE,"E46.0"),sQuery(id+"F5.wireOp",EDGE,"E47.0"),sQuery(id+"F5.wireOp",EDGE,"E48.0"),sQuery(id+"F5.wireOp",EDGE,"E49.0"),sQuery(id+"F5.wireOp",EDGE,"E50.0"),sQuery(id+"F5.wireOp",EDGE,"E51.0"),sQuery(id+"F5.wireOp",EDGE,"E52.0"),sQuery(id+"F5.wireOp",EDGE,"E53.0"),sQuery(id+"F5.wireOp",EDGE,"E54.0"),sQuery(id+"F5.wireOp",EDGE,"E55.0"),sQuery(id+"F5.wireOp",EDGE,"E56.0"),sQuery(id+"F5.wireOp",EDGE,"E57.0")])],"isStart":false});
            cPlane(context, id + "F42", {"entities" : qUnion([Q0]), "cplaneType" : CPlaneType.OFFSET, "offset" : 127 * mm, "width" : 152.4 * mm, "height" : 152.4 * mm});
        }
        {
            var Q0;
            Q0=qCreatedBy(id+"F42.planeOp",FACE);
            var sketch = newSketch(context, id + "F43", { "sketchPlane" : qUnion([Q0])});
            skCircle(sketch, "E109", {"center": v(5.54, 32.2) * mm, "radius": 3.18 * mm});
            skCircle(sketch, "E110", {"center": v(5.54, 32.2) * mm, "radius": 1.52 * mm});
            skSolve(sketch);
        }
        {
            var Q0;
            Q0 = qSketchRegion(id + "F43", true);
            extrude(context, id + "F44", {"entities" : qUnion([Q0]), "depth" : 3.17 * mm});
        }
    });
